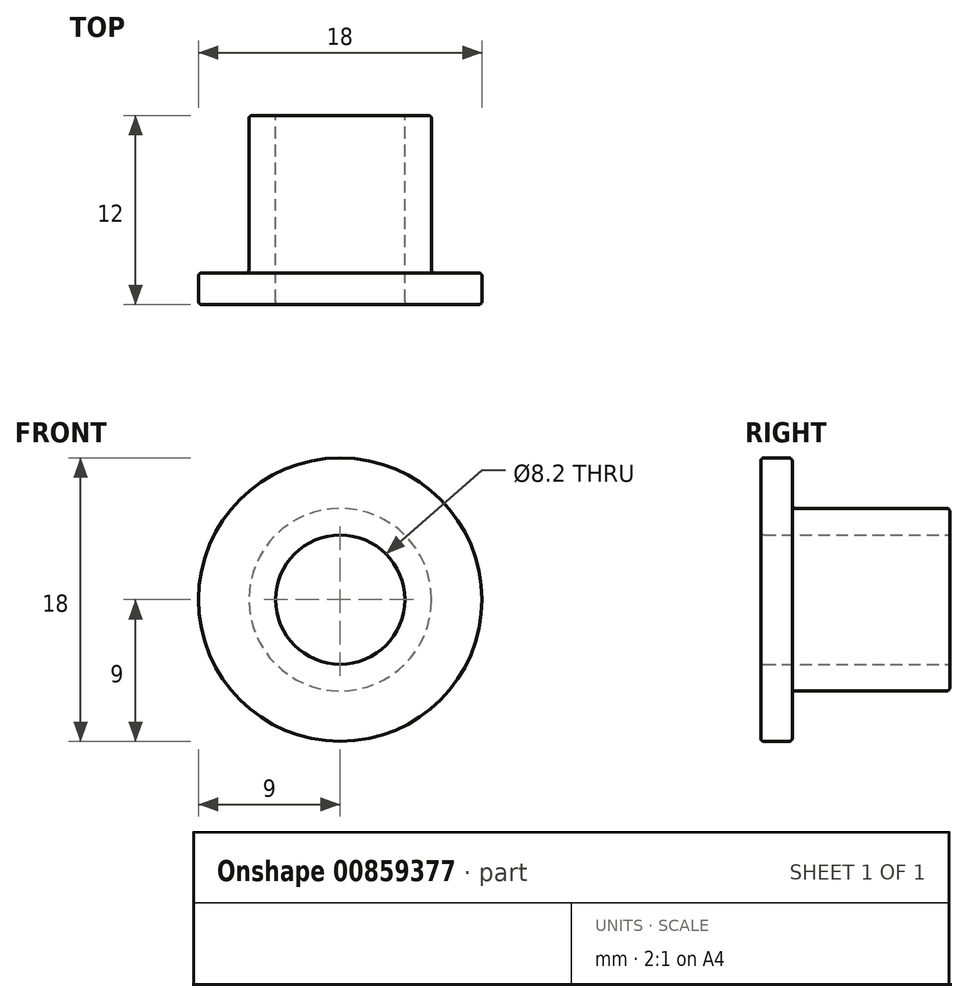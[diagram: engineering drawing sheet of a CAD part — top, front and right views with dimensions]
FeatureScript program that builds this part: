
annotation { "Feature Type Name" : "Feature", "Feature Type Description" : "" }
export const myFeature = defineFeature(function(context is Context, id is Id, definition is map)
    precondition{}
    {
        {
            var Q0;
            Q0=qCreatedBy(makeId("Front.planeOp"),FACE);
            var sketch = newSketch(context, id + "F0", { "sketchPlane" : qUnion([Q0])});
            skCircle(sketch, "E0", {"center": v(0, 0) * mm, "radius": 9 * mm});
            skCircle(sketch, "E1", {"center": v(0, 0) * mm, "radius": 4.1 * mm});
            skCircle(sketch, "E2", {"center": v(0, 0) * mm, "radius": 5.8 * mm});
            skSolve(sketch);
        }
        {
            var Q0;
            Q0=makeQuery(id+"F0.imprint","IMPRINT",FACE,{"disambiguationData":[TD([[makeQuery(id+"F0.imprint","IMPRINT",EDGE,{"derivedFrom":sQuery(id+"F0.wireOp",EDGE,"E0")}),1.0]])]});
            var Q1;
            Q1=makeQuery(id+"F0.imprint","IMPRINT",FACE,{"disambiguationData":[TD([[makeQuery(id+"F0.imprint","IMPRINT",EDGE,{"derivedFrom":sQuery(id+"F0.wireOp",EDGE,"E1")}),-1.0]])]});
            var Q2;
            Q2 = qSketchRegion(id + "FLc32slgWGsnS4D_1", true);
            extrude(context, id + "F1", {"entities" : qUnion([Q0, Q1, Q2]), "depth" : 2 * mm, "offsetDistance" : 25 * mm});
        }
        {
            var Q0;
            Q0=makeQuery(id+"F0.imprint","IMPRINT",FACE,{"disambiguationData":[TD([[makeQuery(id+"F0.imprint","IMPRINT",EDGE,{"derivedFrom":sQuery(id+"F0.wireOp",EDGE,"E1")}),-1.0]])]});
            extrude(context, id + "F2", {"entities" : qUnion([Q0]), "operationType" : NewBodyOperationType.ADD, "depth" : -10 * mm, "offsetDistance" : 25 * mm});
        }
        {
            var Q0;
            Q0=makeQuery(id+"F1.opExtrude","CAP_EDGE",EDGE,{"disambiguationData":[OSD([sQuery(id+"F0.wireOp",EDGE,"E0")])],"isStart":true});
            var Q1;
            Q1=makeQuery(id+"F1.opExtrude","CAP_EDGE",EDGE,{"disambiguationData":[OSD([sQuery(id+"F0.wireOp",EDGE,"E0")])],"isStart":false});
            var Q2;
            Q2=makeQuery(id+"F2.opExtrude","SWEPT_FACE",FACE,{"disambiguationData":[OSD([sQuery(id+"F0.wireOp",EDGE,"E2")])]});
            var Q3;
            Q3=makeQuery(id+"F2.opExtrude","CAP_EDGE",EDGE,{"disambiguationData":[OSD([sQuery(id+"F0.wireOp",EDGE,"E1")])],"isStart":false});
            var Q4;
            Q4=makeQuery(id+"F1.opExtrude","CAP_EDGE",EDGE,{"disambiguationData":[OSD([sQuery(id+"F0.wireOp",EDGE,"E1")])],"isStart":false});
            fillet(context, id + "F3", {"entities" : qUnion([Q0, Q1, Q2, Q3, Q4]), "radius" : 0.2 * mm, "allowEdgeOverflow" : false});
        }
    });
